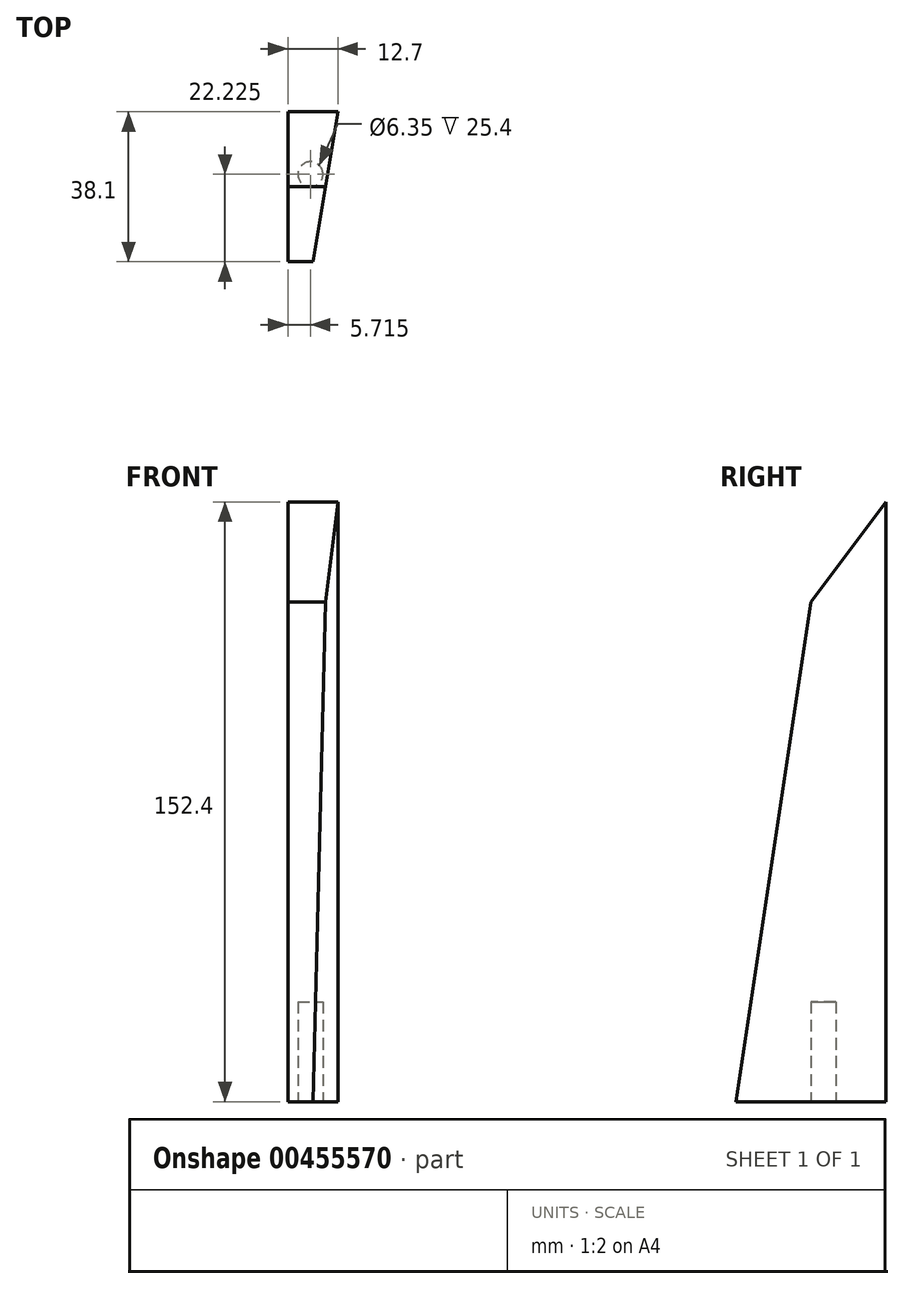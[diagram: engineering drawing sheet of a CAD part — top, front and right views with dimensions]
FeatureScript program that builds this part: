
annotation { "Feature Type Name" : "Feature", "Feature Type Description" : "" }
export const myFeature = defineFeature(function(context is Context, id is Id, definition is map)
    precondition{}
    {
        {
            var Q0;
            Q0=qCreatedBy(makeId("Right.planeOp"),FACE);
            var sketch = newSketch(context, id + "F0", { "sketchPlane" : qUnion([Q0])});
            skLineSegment(sketch, "E0", {"start": v(0, 0) * mm, "end": v(38.1, 0) * mm});
            skLineSegment(sketch, "E1", {"start": v(38.1, 0) * mm, "end": v(38.1, 152.4) * mm});
            skLineSegment(sketch, "E2", {"start": v(38.1, 152.4) * mm, "end": v(19.05, 127) * mm});
            skLineSegment(sketch, "E3", {"start": v(19.05, 127) * mm, "end": v(0, 0) * mm});
            skSolve(sketch);
        }
        {
            var Q0;
            Q0=makeQuery(id+"F0.imprint","IMPRINT",FACE,{"disambiguationData":[TD([[makeQuery(id+"F0.imprint","IMPRINT",EDGE,{"derivedFrom":sQuery(id+"F0.wireOp",EDGE,"E0")}),1.0]])]});
            extrude(context, id + "F1", {"entities" : qUnion([Q0]), "depth" : 12.7 * mm});
        }
        {
            var Q0;
            Q0=makeQuery(id+"F1.opExtrude","SWEPT_FACE",FACE,{"disambiguationData":[OSD([sQuery(id+"F0.wireOp",EDGE,"E0")])]});
            var sketch = newSketch(context, id + "F2", { "sketchPlane" : qUnion([Q0])});
            skPoint(sketch, "E4.centerSnap0", {"position": v(6.35, -38.1) * mm});
            skCircle(sketch, "E5", {"center": v(5.72, -22.22) * mm, "radius": 3.18 * mm});
            skSolve(sketch);
        }
        {
            var Q0;
            Q0=makeQuery(id+"F2.imprint","IMPRINT",FACE,{"disambiguationData":[TD([[makeQuery(id+"F2.imprint","IMPRINT",EDGE,{"derivedFrom":sQuery(id+"F2.wireOp",EDGE,"E5")}),1.0]])]});
            extrude(context, id + "F3", {"entities" : qUnion([Q0]), "operationType" : NewBodyOperationType.REMOVE, "oppositeDirection" : true, "depth" : 25.4 * mm});
        }
        {
            var Q0;
            Q0=makeQuery(id+"F1.opExtrude","SWEPT_FACE",FACE,{"disambiguationData":[OSD([sQuery(id+"F0.wireOp",EDGE,"E0")])]});
            var sketch = newSketch(context, id + "F4", { "sketchPlane" : qUnion([Q0])});
            skLineSegment(sketch, "E6", {"start": v(12.7, -38.1) * mm, "end": v(6.35, 0) * mm});
            skSolve(sketch);
        }
        {
            var Q0;
            {var subQ0=sQuery(id+"F4.wireOp",EDGE,"E6");Q0=makeQuery(id+"F4.imprint","IMPRINT",FACE,{"disambiguationData":[TD([[makeQuery(id+"F4.imprint","IMPRINT",EDGE,{"derivedFrom":subQ0}),-1.0]])]});}
            extrude(context, id + "F5", {"entities" : qUnion([Q0]), "operationType" : NewBodyOperationType.REMOVE, "oppositeDirection" : true, "depth" : 254 * mm});
        }
    });
